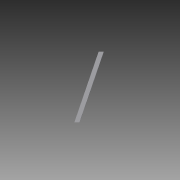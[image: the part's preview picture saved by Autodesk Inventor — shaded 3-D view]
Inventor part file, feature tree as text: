
AUTODESK INVENTOR PART (.ipt)
format: ipt  version: 2015 SP1 (Build 190203100, 203)  size: 121,344 bytes
history: native  units: in
note: dims shown in document units (in); Inventor stores cm internally (conversion verified against a paired STEP export)
features: sketch x5, projected_geometry x4, extrude x3, hole x2
ambient origin geometry x8: Origin, YZ Plane, XZ Plane, XY Plane, X Axis, Y Axis, Z Axis, Center Point
bodies: Solid1 (feature_tree)
feature tree (14):
  extrude  "Extrusion1"  Depth=31.0in
  extrude  "Extrusion4"  TaperAngle=90.0deg  [1 undecoded]
  extrude  "Extrusion6"  TaperAngle=90.0deg  [1 undecoded]
  hole  "Hole3"  [1 undecoded]
  hole  "Hole4"  [1 undecoded]
  sketch  "Sketch1"  dims[d0=20.75in d1=31.0in]
  sketch  "Sketch6"  dims[d2=2.0in d3=90.0deg]
  projected_geometry  "Projected Loop5"
  sketch  "Sketch8"  dims[d4=2.0in d5=90.0deg]
  projected_geometry  "Projected Loop7"
  sketch  "Sketch9"  dims[d6=0.125in d7=0.0in d33=135.0deg]
  projected_geometry  "Projected Loop8"
  sketch  "Sketch10"  dims[d34=0.125in d35=0.0in d38=0.125in d39=0.0in d40=0.5in d41=0.375in d42=0.25in d43=0.75in d44=0.375in d45=0.25in d46=0.5635in d47=1.0in d48=0.8108in d52=0.5in d53=1.0in d54=0.25in d55=0.75in d56=0.375in d57=0.25in d58=0.5635in d59=1.0in d60=0.8108in]
  projected_geometry  "Projected Loop9"
note: 4 required parameter values undecoded (feature->parameter linkage not recoverable at this tier; creation-order binding heuristic only, values carry confidence <= 0.55)
